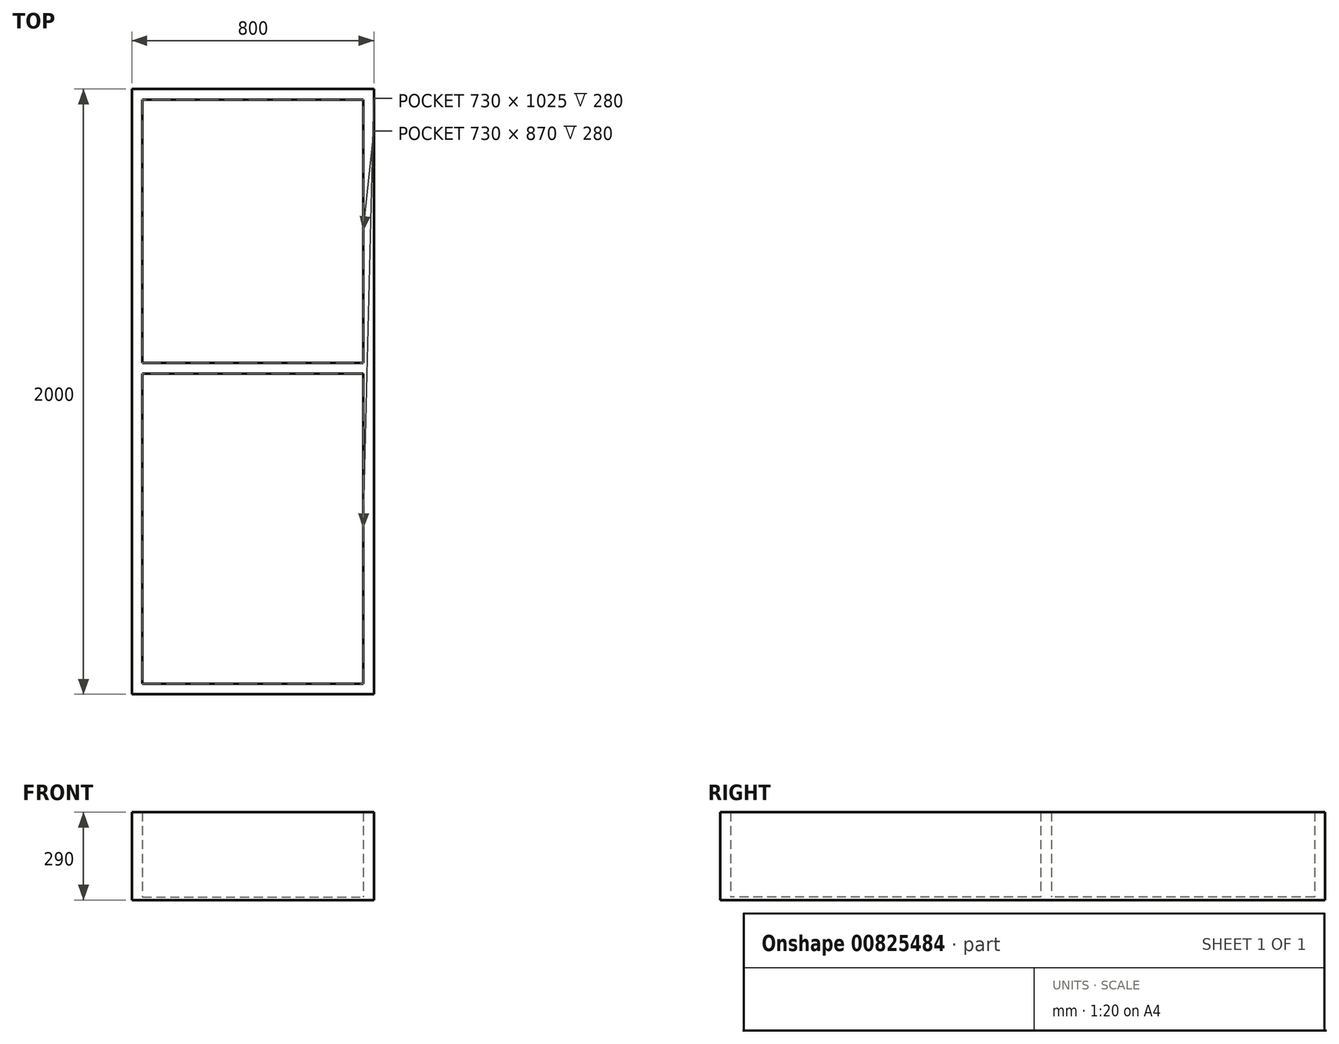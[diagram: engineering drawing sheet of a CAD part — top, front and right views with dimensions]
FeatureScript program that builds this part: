
annotation { "Feature Type Name" : "Feature", "Feature Type Description" : "" }
export const myFeature = defineFeature(function(context is Context, id is Id, definition is map)
    precondition{}
    {
        {
            var Q0;
            Q0=qCreatedBy(makeId("Top.planeOp"),FACE);
            var sketch = newSketch(context, id + "F0", { "sketchPlane" : qUnion([Q0])});
            skLineSegment(sketch, "E0.bottom", {"start": v(400, 1000) * mm, "end": v(-400, 1000) * mm});
            skLineSegment(sketch, "E0.top", {"start": v(400, -1000) * mm, "end": v(-400, -1000) * mm});
            skLineSegment(sketch, "E0.left", {"start": v(400, 1000) * mm, "end": v(400, -1000) * mm});
            skLineSegment(sketch, "E0.right", {"start": v(-400, 1000) * mm, "end": v(-400, -1000) * mm});
            skPoint(sketch, "E0.middle", {"position": v(0, 0) * mm});
            skLineSegment(sketch, "E1.0", {"start": v(-365, 965) * mm, "end": v(-365, 95) * mm});
            skLineSegment(sketch, "E1.1", {"start": v(365, 965) * mm, "end": v(-365, 965) * mm});
            skLineSegment(sketch, "E1.2", {"start": v(365, 965) * mm, "end": v(365, 95) * mm});
            skLineSegment(sketch, "E1.3", {"start": v(365, -965) * mm, "end": v(-365, -965) * mm});
            skLineSegment(sketch, "E2", {"start": v(-365, 95) * mm, "end": v(365, 95) * mm});
            skLineSegment(sketch, "E3.0", {"start": v(-365, 60) * mm, "end": v(365, 60) * mm});
            skLineSegment(sketch, "E4.trimOffspring", {"start": v(-365, 60) * mm, "end": v(-365, -965) * mm});
            skLineSegment(sketch, "E5.trimOffspring", {"start": v(365, 60) * mm, "end": v(365, -965) * mm});
            skSolve(sketch);
        }
        {
            var Q0;
            Q0 = qSketchRegion(id + "F0", true);
            extrude(context, id + "F1", {"entities" : qUnion([Q0]), "depth" : 280 * mm, "offsetDistance" : 25 * mm});
        }
        {
            var Q0;
            Q0=makeQuery(id+"F1.opExtrude","CAP_FACE",FACE,{"disambiguationData":[OSD([sQuery(id+"F0.wireOp",EDGE,"E0.bottom"),sQuery(id+"F0.wireOp",EDGE,"E0.top"),sQuery(id+"F0.wireOp",EDGE,"E0.left"),sQuery(id+"F0.wireOp",EDGE,"E0.right"),sQuery(id+"F0.wireOp",EDGE,"E1.0"),sQuery(id+"F0.wireOp",EDGE,"E1.1"),sQuery(id+"F0.wireOp",EDGE,"E1.2"),sQuery(id+"F0.wireOp",EDGE,"E1.3"),sQuery(id+"F0.wireOp",EDGE,"E2"),sQuery(id+"F0.wireOp",EDGE,"E3.0"),sQuery(id+"F0.wireOp",EDGE,"E4.trimOffspring"),sQuery(id+"F0.wireOp",EDGE,"E5.trimOffspring")])],"isStart":true});
            var sketch = newSketch(context, id + "F2", { "sketchPlane" : qUnion([Q0])});
            skLineSegment(sketch, "E6.bottom", {"start": v(400, 1000) * mm, "end": v(-400, 1000) * mm});
            skLineSegment(sketch, "E6.top", {"start": v(400, -1000) * mm, "end": v(-400, -1000) * mm});
            skLineSegment(sketch, "E6.left", {"start": v(400, 1000) * mm, "end": v(400, -1000) * mm});
            skLineSegment(sketch, "E6.right", {"start": v(-400, 1000) * mm, "end": v(-400, -1000) * mm});
            skSolve(sketch);
        }
        {
            var Q0;
            Q0 = qSketchRegion(id + "F2", true);
            extrude(context, id + "F3", {"entities" : qUnion([Q0]), "operationType" : NewBodyOperationType.ADD, "depth" : 10 * mm, "offsetDistance" : 25 * mm});
        }
    });
